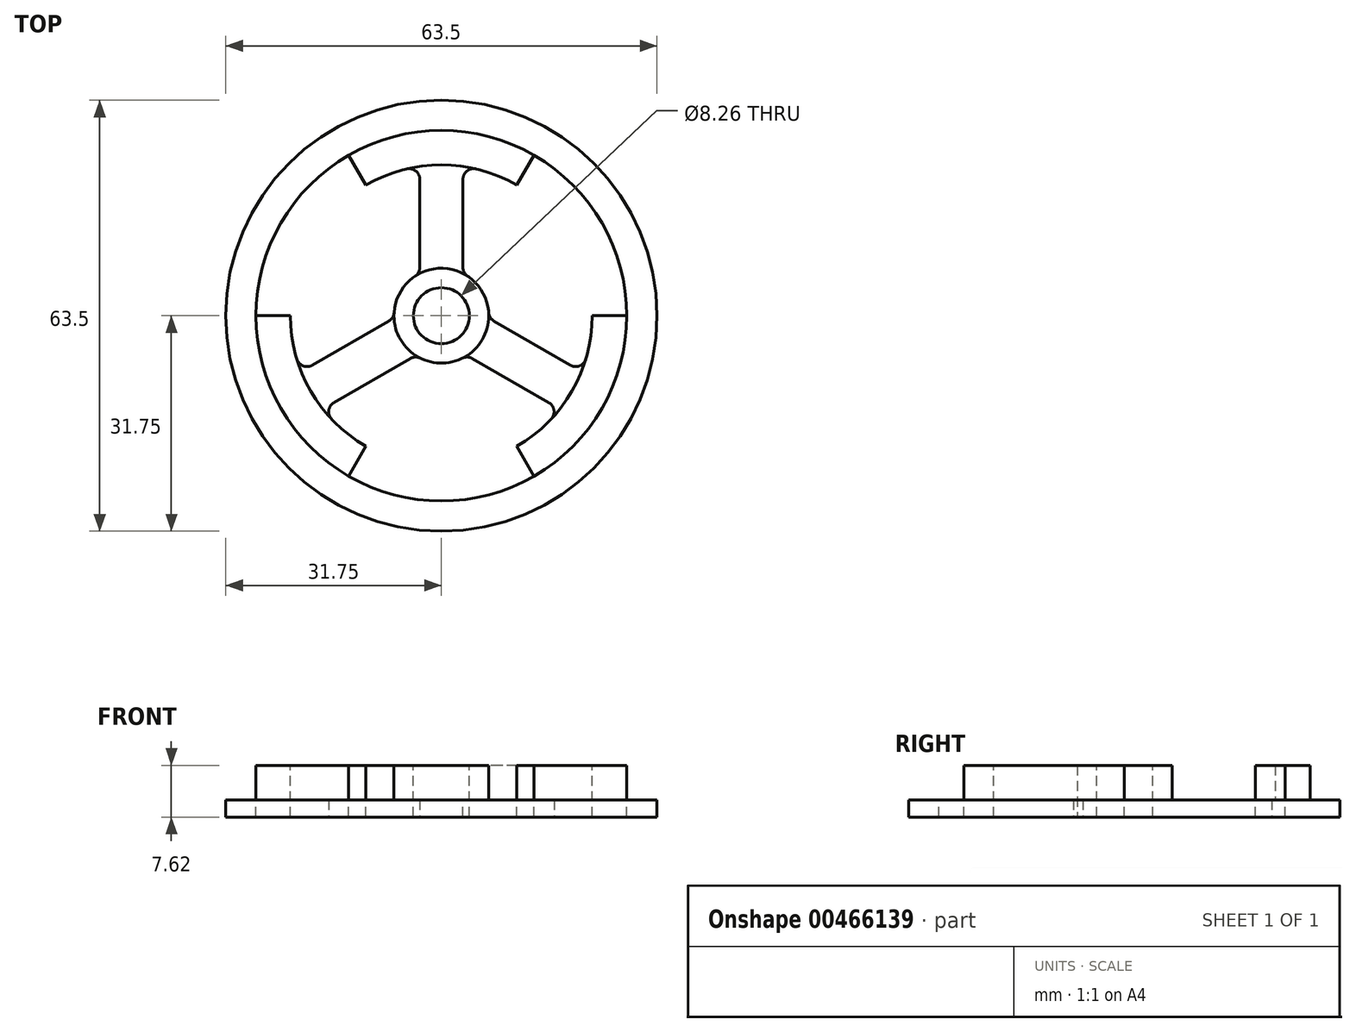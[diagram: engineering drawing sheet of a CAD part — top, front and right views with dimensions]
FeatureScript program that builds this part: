
annotation { "Feature Type Name" : "Feature", "Feature Type Description" : "" }
export const myFeature = defineFeature(function(context is Context, id is Id, definition is map)
    precondition{}
    {
        {
            var Q0;
            Q0=qCreatedBy(makeId("Top.planeOp"),FACE);
            var sketch = newSketch(context, id + "F0", { "sketchPlane" : qUnion([Q0])});
            skCircle(sketch, "E0", {"center": v(0, 0) * mm, "radius": 31.75 * mm});
            skSolve(sketch);
        }
        {
            var Q0;
            Q0=makeQuery(id+"F0.imprint","IMPRINT",FACE,{"disambiguationData":[TD([[makeQuery(id+"F0.imprint","IMPRINT",EDGE,{"derivedFrom":sQuery(id+"F0.wireOp",EDGE,"E0")}),1.0]])]});
            extrude(context, id + "F1", {"entities" : qUnion([Q0]), "depth" : 2.54 * mm});
        }
        {
            var Q0;
            Q0=makeQuery(id+"F1.opExtrude","CAP_FACE",FACE,{"disambiguationData":[OSD([sQuery(id+"F0.wireOp",EDGE,"E0")])],"isStart":false});
            var sketch = newSketch(context, id + "F2", { "sketchPlane" : qUnion([Q0])});
            skCircle(sketch, "E1", {"center": v(0, 0) * mm, "radius": 27.3 * mm});
            skCircle(sketch, "E2.0", {"center": v(0, 0) * mm, "radius": 22.23 * mm});
            skCircle(sketch, "E3", {"center": v(0, 0) * mm, "radius": 6.99 * mm});
            skSolve(sketch);
        }
        {
            var Q0;
            Q0=makeQuery(id+"F2.imprint","IMPRINT",FACE,{"disambiguationData":[TD([[makeQuery(id+"F2.imprint","IMPRINT",EDGE,{"derivedFrom":sQuery(id+"F2.wireOp",EDGE,"E3")}),1.0]])]});
            var Q1;
            Q1=makeQuery(id+"F2.imprint","IMPRINT",FACE,{"disambiguationData":[TD([[makeQuery(id+"F2.imprint","IMPRINT",EDGE,{"derivedFrom":sQuery(id+"F2.wireOp",EDGE,"E1")}),1.0]])]});
            extrude(context, id + "F3", {"entities" : qUnion([Q0, Q1]), "operationType" : NewBodyOperationType.ADD, "depth" : 5.08 * mm});
        }
        {
            var Q0;
            Q0=makeQuery(id+"F3.opExtrude","CAP_FACE",FACE,{"disambiguationData":[OSD([sQuery(id+"F2.wireOp",EDGE,"E3")])],"isStart":false});
            var sketch = newSketch(context, id + "F4", { "sketchPlane" : qUnion([Q0])});
            skCircle(sketch, "E4", {"center": v(0, 0) * mm, "radius": 4.13 * mm});
            skSolve(sketch);
        }
        {
            var Q0;
            Q0=makeQuery(id+"F4.imprint","IMPRINT",FACE,{"disambiguationData":[TD([[makeQuery(id+"F4.imprint","IMPRINT",EDGE,{"derivedFrom":sQuery(id+"F4.wireOp",EDGE,"E4")}),1.0]])]});
            extrude(context, id + "F5", {"entities" : qUnion([Q0]), "operationType" : NewBodyOperationType.REMOVE, "oppositeDirection" : true, "depth" : 25.4 * mm, "hasSecondDirection" : true, "secondDirectionBound" : SecondDirectionBoundingType.THROUGH_ALL, "secondDirectionOppositeDirection" : false, "secondDirectionDepth" : 25.4 * mm});
        }
        {
            var Q0;
            Q0=makeQuery(id+"F3.boolean.opBoolean","SPLIT",FACE,{"disambiguationData":[TD([makeQuery(id+"F3.opExtrude","SWEPT_FACE",FACE,{"disambiguationData":[OSD([sQuery(id+"F2.wireOp",EDGE,"E2.0")])]})])],"derivedFrom":makeQuery(id+"F1.opExtrude","CAP_FACE",FACE,{"disambiguationData":[OSD([sQuery(id+"F0.wireOp",EDGE,"E0")])],"isStart":false})});
            var sketch = newSketch(context, id + "F6", { "sketchPlane" : qUnion([Q0])});
            skPoint(sketch, "E5.center", {"position": v(0, 0) * mm});
            skLineSegment(sketch, "E6.0", {"start": v(3.18, 6.22) * mm, "end": v(3.18, 22) * mm});
            skLineSegment(sketch, "E7.0", {"start": v(3.8, -5.86) * mm, "end": v(17.46, -13.75) * mm});
            skArc(sketch, "E8", {"start": v(-17.46, -13.75) * mm, "mid": v(0, -22.22) * mm, "end": v(17.46, -13.75) * mm});
            skLineSegment(sketch, "E9.trimOffspring", {"start": v(6.98, -0.36) * mm, "end": v(20.64, -8.25) * mm});
            skLineSegment(sketch, "E10.trimOffspring", {"start": v(-3.18, 6.22) * mm, "end": v(-3.18, 22) * mm});
            skLineSegment(sketch, "E11.trimOffspring", {"start": v(-6.98, -0.36) * mm, "end": v(-20.64, -8.25) * mm});
            skLineSegment(sketch, "E12.trimOffspring", {"start": v(-3.8, -5.86) * mm, "end": v(-17.46, -13.75) * mm});
            skArc(sketch, "E13.trimOffspring", {"start": v(-3.17, 22) * mm, "mid": v(-19.25, 11.11) * mm, "end": v(-20.64, -8.25) * mm});
            skArc(sketch, "E14.trimOffspring", {"start": v(20.64, -8.25) * mm, "mid": v(19.25, 11.11) * mm, "end": v(3.18, 22) * mm});
            skArc(sketch, "E15", {"start": v(6.98, -0.36) * mm, "mid": v(6.05, 3.5) * mm, "end": v(3.18, 6.22) * mm});
            skPoint(sketch, "E16.orphan", {"position": v(6.35, 0) * mm});
            skArc(sketch, "E17.trimOffspring", {"start": v(-3.8, -5.86) * mm, "mid": v(0, -6.99) * mm, "end": v(3.8, -5.86) * mm});
            skArc(sketch, "E18.trimOffspring", {"start": v(-3.17, 6.22) * mm, "mid": v(-6.05, 3.5) * mm, "end": v(-6.98, -0.36) * mm});
            skSolve(sketch);
        }
        {
            var Q0;
            {var subQ0=sQuery(id+"F6.wireOp",EDGE,"E6.0");Q0=makeQuery(id+"F6.imprint","IMPRINT",FACE,{"disambiguationData":[TD([[makeQuery(id+"F6.imprint","IMPRINT",EDGE,{"derivedFrom":subQ0}),-1.0]])]});}
            var Q1;
            {var subQ0=sQuery(id+"F6.wireOp",EDGE,"E7.0");Q1=makeQuery(id+"F6.imprint","IMPRINT",FACE,{"disambiguationData":[TD([[makeQuery(id+"F6.imprint","IMPRINT",EDGE,{"derivedFrom":subQ0}),-1.0]])]});}
            var Q2;
            {var subQ0=sQuery(id+"F6.wireOp",EDGE,"E10.trimOffspring");Q2=makeQuery(id+"F6.imprint","IMPRINT",FACE,{"disambiguationData":[TD([[makeQuery(id+"F6.imprint","IMPRINT",EDGE,{"derivedFrom":subQ0}),1.0]])]});}
            extrude(context, id + "F7", {"entities" : qUnion([Q0, Q1, Q2]), "operationType" : NewBodyOperationType.REMOVE, "oppositeDirection" : true, "depth" : 25.4 * mm, "hasSecondDirection" : true, "secondDirectionBound" : SecondDirectionBoundingType.THROUGH_ALL, "secondDirectionOppositeDirection" : false, "secondDirectionDepth" : 25.4 * mm});
        }
        {
            var Q0;
            Q0=makeQuery(id+"F7.boolean.opBoolean","COPY",EDGE,{"derivedFrom":makeQuery(id+"F7.opExtrude","SWEPT_EDGE",EDGE,{"disambiguationData":[OSD([sQuery(id+"F2.wireOp",EDGE,"E2.0"),sQuery(id+"F6.wireOp",EDGE,"E7.0"),sQuery(id+"F6.wireOp",EDGE,"E8")])]})});
            var Q1;
            Q1=makeQuery(id+"F7.boolean.opBoolean","COPY",EDGE,{"derivedFrom":makeQuery(id+"F7.opExtrude","SWEPT_EDGE",EDGE,{"disambiguationData":[OSD([sQuery(id+"F2.wireOp",EDGE,"E2.0"),sQuery(id+"F6.wireOp",EDGE,"E9.trimOffspring"),sQuery(id+"F6.wireOp",EDGE,"E14.trimOffspring")])]})});
            var Q2;
            Q2=makeQuery(id+"F7.boolean.opBoolean","COPY",EDGE,{"derivedFrom":makeQuery(id+"F7.opExtrude","SWEPT_EDGE",EDGE,{"disambiguationData":[OSD([sQuery(id+"F6.wireOp",EDGE,"gMmunLFY-C7J5-eRmg-KZBp-dYpe1jPGCkla"),sQuery(id+"F6.wireOp",EDGE,"E9.trimOffspring")])]})});
            var Q3;
            Q3=makeQuery(id+"F7.boolean.opBoolean","COPY",EDGE,{"derivedFrom":makeQuery(id+"F7.opExtrude","SWEPT_EDGE",EDGE,{"disambiguationData":[OSD([sQuery(id+"F6.wireOp",EDGE,"E6.0"),sQuery(id+"F6.wireOp",EDGE,"gMmunLFY-C7J5-eRmg-KZBp-dYpe1jPGCkla")])]})});
            var Q4;
            Q4=makeQuery(id+"F7.boolean.opBoolean","COPY",EDGE,{"derivedFrom":makeQuery(id+"F7.opExtrude","SWEPT_EDGE",EDGE,{"disambiguationData":[OSD([sQuery(id+"F6.wireOp",EDGE,"gMmunLFY-C7J5-eRmg-KZBp-dYpe1jPGCkla"),sQuery(id+"F6.wireOp",EDGE,"E10.trimOffspring")])]})});
            var Q5;
            Q5=makeQuery(id+"F7.boolean.opBoolean","COPY",EDGE,{"derivedFrom":makeQuery(id+"F7.opExtrude","SWEPT_EDGE",EDGE,{"disambiguationData":[OSD([sQuery(id+"F6.wireOp",EDGE,"gMmunLFY-C7J5-eRmg-KZBp-dYpe1jPGCkla"),sQuery(id+"F6.wireOp",EDGE,"E11.trimOffspring")])]})});
            var Q6;
            Q6=makeQuery(id+"F7.boolean.opBoolean","COPY",EDGE,{"derivedFrom":makeQuery(id+"F7.opExtrude","SWEPT_EDGE",EDGE,{"disambiguationData":[OSD([sQuery(id+"F6.wireOp",EDGE,"gMmunLFY-C7J5-eRmg-KZBp-dYpe1jPGCkla"),sQuery(id+"F6.wireOp",EDGE,"E12.trimOffspring")])]})});
            var Q7;
            Q7=makeQuery(id+"F7.boolean.opBoolean","COPY",EDGE,{"derivedFrom":makeQuery(id+"F7.opExtrude","SWEPT_EDGE",EDGE,{"disambiguationData":[OSD([sQuery(id+"F6.wireOp",EDGE,"E7.0"),sQuery(id+"F6.wireOp",EDGE,"gMmunLFY-C7J5-eRmg-KZBp-dYpe1jPGCkla")])]})});
            var Q8;
            Q8=makeQuery(id+"F7.boolean.opBoolean","COPY",EDGE,{"derivedFrom":makeQuery(id+"F7.opExtrude","SWEPT_EDGE",EDGE,{"disambiguationData":[OSD([sQuery(id+"F2.wireOp",EDGE,"E2.0"),sQuery(id+"F6.wireOp",EDGE,"E6.0"),sQuery(id+"F6.wireOp",EDGE,"E14.trimOffspring")])]})});
            var Q9;
            Q9=makeQuery(id+"F7.boolean.opBoolean","COPY",EDGE,{"derivedFrom":makeQuery(id+"F7.opExtrude","SWEPT_EDGE",EDGE,{"disambiguationData":[OSD([sQuery(id+"F2.wireOp",EDGE,"E2.0"),sQuery(id+"F6.wireOp",EDGE,"E10.trimOffspring"),sQuery(id+"F6.wireOp",EDGE,"E13.trimOffspring")])]})});
            var Q10;
            Q10=makeQuery(id+"F7.boolean.opBoolean","COPY",EDGE,{"derivedFrom":makeQuery(id+"F7.opExtrude","SWEPT_EDGE",EDGE,{"disambiguationData":[OSD([sQuery(id+"F2.wireOp",EDGE,"E2.0"),sQuery(id+"F6.wireOp",EDGE,"E11.trimOffspring"),sQuery(id+"F6.wireOp",EDGE,"E13.trimOffspring")])]})});
            var Q11;
            Q11=makeQuery(id+"F7.boolean.opBoolean","COPY",EDGE,{"derivedFrom":makeQuery(id+"F7.opExtrude","SWEPT_EDGE",EDGE,{"disambiguationData":[OSD([sQuery(id+"F2.wireOp",EDGE,"E2.0"),sQuery(id+"F6.wireOp",EDGE,"E8"),sQuery(id+"F6.wireOp",EDGE,"E12.trimOffspring")])]})});
            fillet(context, id + "F8", {"entities" : qUnion([Q0, Q1, Q2, Q3, Q4, Q5, Q6, Q7, Q8, Q9, Q10, Q11]), "radius" : 1.59 * mm, "tangentPropagation" : true, "allowEdgeOverflow" : false});
        }
        {
            var Q0;
            Q0=makeQuery(id+"F3.opExtrude","CAP_FACE",FACE,{"disambiguationData":[OSD([sQuery(id+"F2.wireOp",EDGE,"E1"),sQuery(id+"F2.wireOp",EDGE,"E2.0")])],"isStart":false});
            var sketch = newSketch(context, id + "F9", { "sketchPlane" : qUnion([Q0])});
            skLineSegment(sketch, "E19.1.0", {"start": v(-11.11, 19.25) * mm, "end": v(-13.65, 23.65) * mm});
            skLineSegment(sketch, "E19.3.0", {"start": v(-22.23, 0) * mm, "end": v(-27.3, 0) * mm});
            skLineSegment(sketch, "E19.5.0", {"start": v(-11.11, -19.25) * mm, "end": v(-13.65, -23.65) * mm});
            skLineSegment(sketch, "E19.7.0", {"start": v(11.11, -19.25) * mm, "end": v(13.65, -23.65) * mm});
            skLineSegment(sketch, "E19.9.0", {"start": v(22.23, 0) * mm, "end": v(27.3, 0) * mm});
            skLineSegment(sketch, "E19.11.0", {"start": v(11.11, 19.25) * mm, "end": v(13.65, 23.65) * mm});
            skPoint(sketch, "E19.center", {"position": v(0, 0) * mm});
            skArc(sketch, "E20", {"start": v(-13.65, 23.65) * mm, "mid": v(-23.65, 13.65) * mm, "end": v(-27.3, 0) * mm});
            skArc(sketch, "E21", {"start": v(-11.11, 19.25) * mm, "mid": v(-19.25, 11.11) * mm, "end": v(-22.23, 0) * mm});
            skArc(sketch, "E22.trimOffspring", {"start": v(-11.11, -19.25) * mm, "mid": v(0, -22.23) * mm, "end": v(11.11, -19.25) * mm});
            skArc(sketch, "E23.trimOffspring", {"start": v(-13.65, -23.65) * mm, "mid": v(0, -27.3) * mm, "end": v(13.65, -23.65) * mm});
            skArc(sketch, "E24.trimOffspring", {"start": v(27.3, 0) * mm, "mid": v(23.65, 13.65) * mm, "end": v(13.65, 23.65) * mm});
            skArc(sketch, "E25.trimOffspring", {"start": v(22.23, 0) * mm, "mid": v(19.25, 11.11) * mm, "end": v(11.11, 19.25) * mm});
            skSolve(sketch);
        }
        {
            var Q0;
            Q0=makeQuery(id+"F9.imprint","IMPRINT",FACE,{"disambiguationData":[TD([[makeQuery(id+"F9.imprint","IMPRINT",EDGE,{"derivedFrom":sQuery(id+"F9.wireOp",EDGE,"E19.9.0")}),1.0]])]});
            var Q1;
            Q1=makeQuery(id+"F9.imprint","IMPRINT",FACE,{"disambiguationData":[TD([[makeQuery(id+"F9.imprint","IMPRINT",EDGE,{"derivedFrom":sQuery(id+"F9.wireOp",EDGE,"E19.5.0")}),1.0]])]});
            var Q2;
            Q2=makeQuery(id+"F9.imprint","IMPRINT",FACE,{"disambiguationData":[TD([[makeQuery(id+"F9.imprint","IMPRINT",EDGE,{"derivedFrom":sQuery(id+"F9.wireOp",EDGE,"E19.1.0")}),1.0]])]});
            extrude(context, id + "F10", {"entities" : qUnion([Q0, Q1, Q2]), "operationType" : NewBodyOperationType.REMOVE, "oppositeDirection" : true, "depth" : 25.4 * mm});
        }
    });
